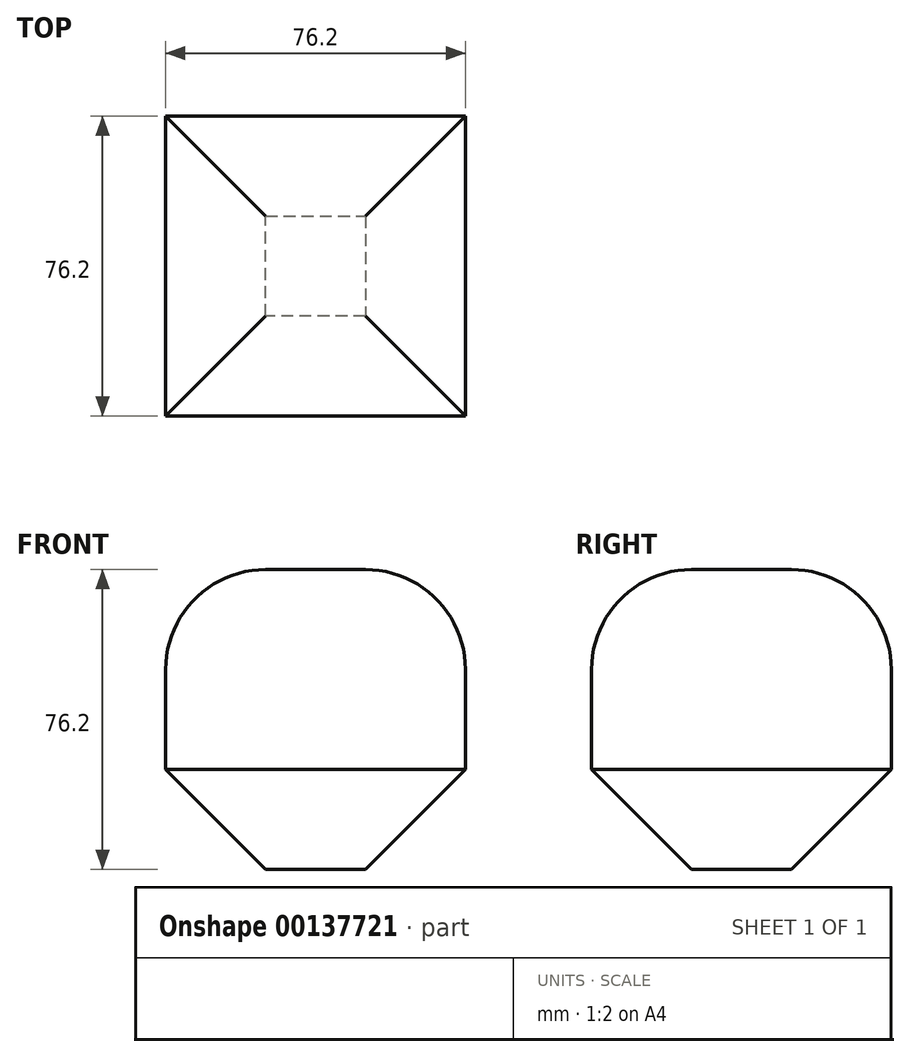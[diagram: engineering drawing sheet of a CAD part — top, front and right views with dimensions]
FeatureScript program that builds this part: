
annotation { "Feature Type Name" : "Feature", "Feature Type Description" : "" }
export const myFeature = defineFeature(function(context is Context, id is Id, definition is map)
    precondition{}
    {
        {
            var Q0;
            Q0=qCreatedBy(makeId("Front.planeOp"),FACE);
            var sketch = newSketch(context, id + "F0", { "sketchPlane" : qUnion([Q0])});
            skLineSegment(sketch, "E0.bottom", {"start": v(76.2, 76.2) * mm, "end": v(0, 76.2) * mm});
            skLineSegment(sketch, "E0.top", {"start": v(76.2, 0) * mm, "end": v(0, 0) * mm});
            skLineSegment(sketch, "E0.left", {"start": v(76.2, 76.2) * mm, "end": v(76.2, 0) * mm});
            skLineSegment(sketch, "E0.right", {"start": v(0, 76.2) * mm, "end": v(0, 0) * mm});
            skSolve(sketch);
        }
        {
            var Q0;
            Q0=makeQuery(id+"F0.imprint","IMPRINT",FACE,{"disambiguationData":[TD([[makeQuery(id+"F0.imprint","IMPRINT",EDGE,{"derivedFrom":sQuery(id+"F0.wireOp",EDGE,"E0.bottom")}),1.0]])]});
            extrude(context, id + "F1", {"entities" : qUnion([Q0]), "depth" : 76.2 * mm});
        }
        {
            var Q0;
            Q0=makeQuery(id+"F1.opExtrude","SWEPT_FACE",FACE,{"disambiguationData":[OSD([sQuery(id+"F0.wireOp",EDGE,"E0.top")])]});
            chamfer(context, id + "F2", {"entities" : qUnion([Q0]), "width" : 25.4 * mm, "tangentPropagation" : true});
        }
        {
            var Q0;
            Q0=makeQuery(id+"F1.opExtrude","SWEPT_FACE",FACE,{"disambiguationData":[OSD([sQuery(id+"F0.wireOp",EDGE,"E0.bottom")])]});
            fillet(context, id + "F3", {"entities" : qUnion([Q0]), "radius" : 25.4 * mm, "tangentPropagation" : true, "allowEdgeOverflow" : false});
        }
    });
